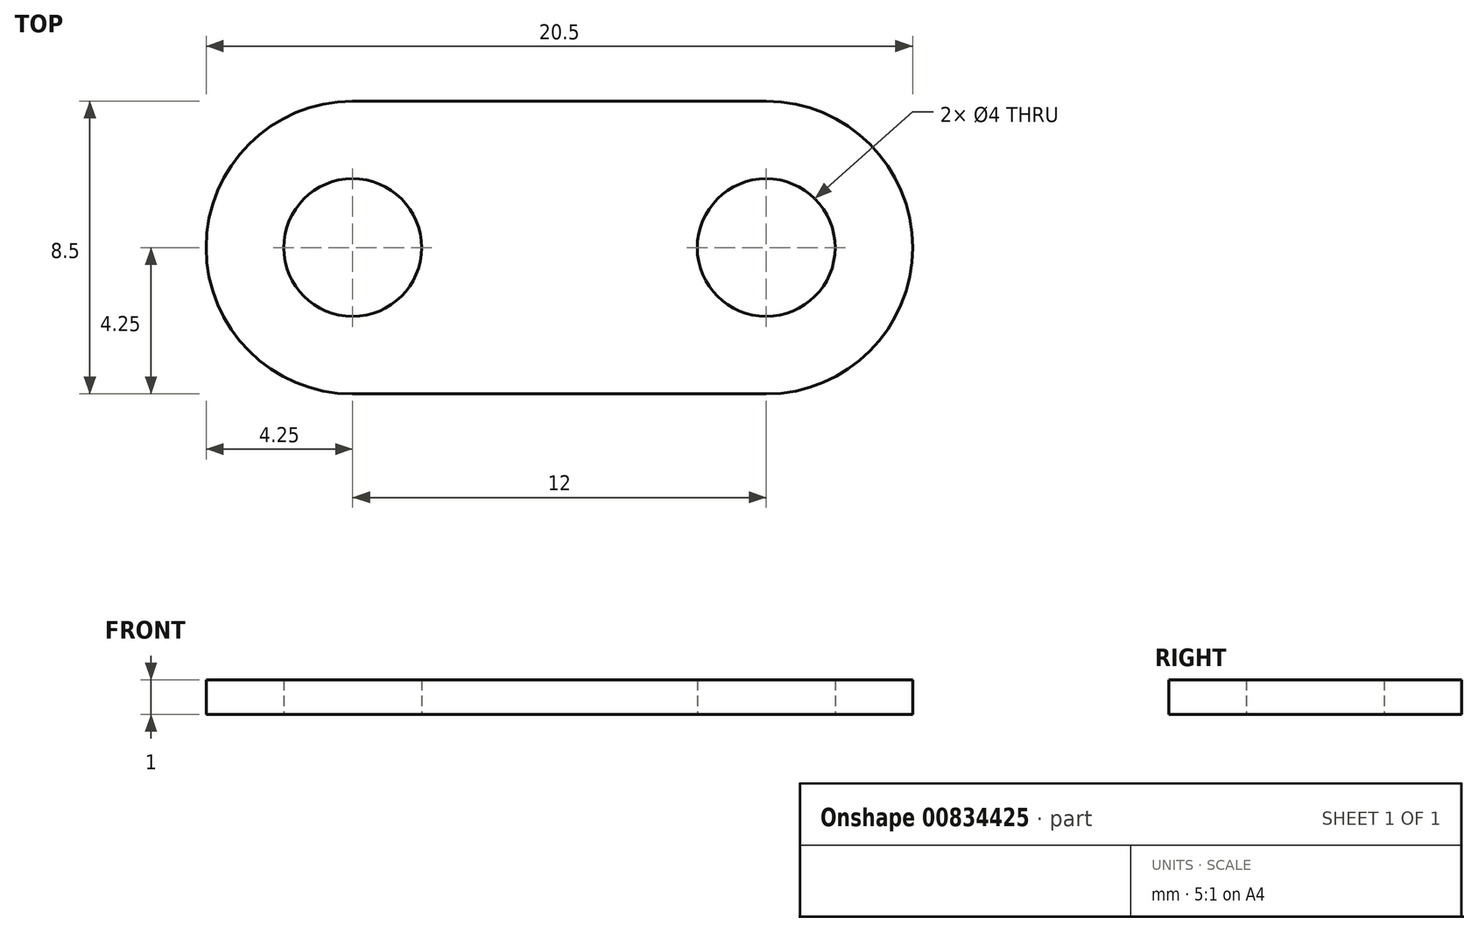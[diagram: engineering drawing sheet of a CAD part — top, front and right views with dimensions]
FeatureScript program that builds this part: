
annotation { "Feature Type Name" : "Feature", "Feature Type Description" : "" }
export const myFeature = defineFeature(function(context is Context, id is Id, definition is map)
    precondition{}
    {
        {
            var Q0;
            Q0=qCreatedBy(makeId("Top.planeOp"),FACE);
            var sketch = newSketch(context, id + "F0", { "sketchPlane" : qUnion([Q0])});
            skLineSegment(sketch, "E0", {"start": v(-6, -4.25) * mm, "end": v(6, -4.25) * mm});
            skLineSegment(sketch, "E1", {"start": v(-6, 4.25) * mm, "end": v(6, 4.25) * mm});
            skArc(sketch, "E2", {"start": v(-6, 4.25) * mm, "mid": v(-10.25, 0) * mm, "end": v(-6, -4.25) * mm});
            skArc(sketch, "E3", {"start": v(6, -4.25) * mm, "mid": v(10.25, 0) * mm, "end": v(6, 4.25) * mm});
            skPoint(sketch, "E4", {"position": v(0, 4.25) * mm});
            skSolve(sketch);
        }
        {
            var Q0;
            Q0=makeQuery(id+"F0.imprint","IMPRINT",FACE,{"disambiguationData":[TD([[makeQuery(id+"F0.imprint","IMPRINT",EDGE,{"derivedFrom":sQuery(id+"F0.wireOp",EDGE,"E0")}),1.0]])]});
            extrude(context, id + "F1", {"entities" : qUnion([Q0]), "depth" : 1 * mm, "offsetDistance" : 25 * mm});
        }
        {
            var Q0;
            Q0=sQuery(id+"F0.wireOp",VERTEX,"E2.center");
            var Q1;
            Q1=sQuery(id+"F0.wireOp",VERTEX,"E3.center");
            var Q2;
            Q2=makeQuery(id+"F1.opExtrude","SWEPT_BODY",BODY,{"disambiguationData":[OSD([sQuery(id+"F0.wireOp",EDGE,"E0"),sQuery(id+"F0.wireOp",EDGE,"E1"),sQuery(id+"F0.wireOp",EDGE,"E2"),sQuery(id+"F0.wireOp",EDGE,"E3")])]});
            hole(context, id + "F2", {"style" : HoleStyle.SIMPLE, "endStyle" : HoleEndStyle.BLIND, "oppositeDirection" : true, "holeDiameter" : 4 * mm, "majorDiameter" : 5 * mm, "holeDepth" : 20 * mm, "tappedDepth" : 12 * mm, "tapClearance" : 3, "locations" : qUnion([Q0, Q1]), "scope" : qUnion([Q2])});
        }
    });
